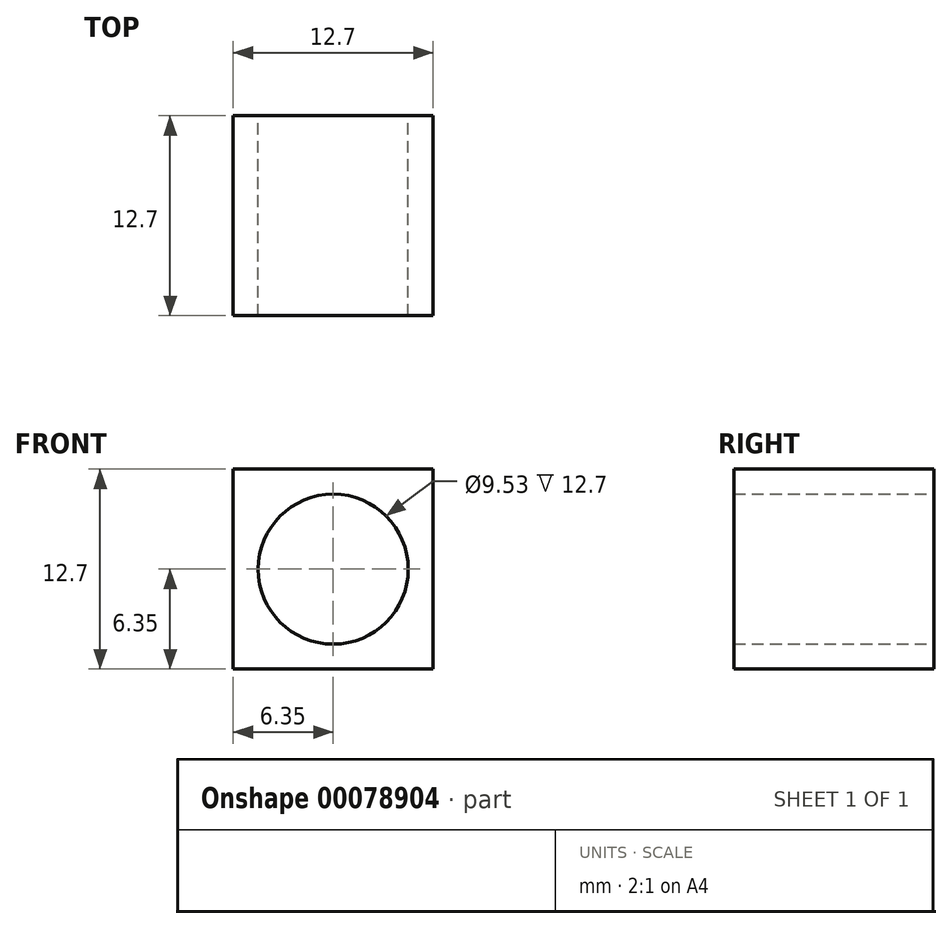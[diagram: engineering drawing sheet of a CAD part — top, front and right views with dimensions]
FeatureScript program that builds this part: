
annotation { "Feature Type Name" : "Feature", "Feature Type Description" : "" }
export const myFeature = defineFeature(function(context is Context, id is Id, definition is map)
    precondition{}
    {
        {
            var Q0;
            Q0=qCreatedBy(makeId("Front.planeOp"),FACE);
            var sketch = newSketch(context, id + "F0", { "sketchPlane" : qUnion([Q0])});
            skLineSegment(sketch, "E0.bottom", {"start": v(-6.35, 6.35) * mm, "end": v(6.35, 6.35) * mm});
            skLineSegment(sketch, "E0.top", {"start": v(-6.35, -6.35) * mm, "end": v(6.35, -6.35) * mm});
            skLineSegment(sketch, "E0.left", {"start": v(-6.35, 6.35) * mm, "end": v(-6.35, -6.35) * mm});
            skLineSegment(sketch, "E0.right", {"start": v(6.35, 6.35) * mm, "end": v(6.35, -6.35) * mm});
            skPoint(sketch, "E0.middle", {"position": v(0, 0) * mm});
            skCircle(sketch, "E1", {"center": v(0, 0) * mm, "radius": 4.76 * mm});
            skSolve(sketch);
        }
        {
            var Q0;
            Q0 = qSketchRegion(id + "F0", true);
            extrude(context, id + "F1", {"entities" : qUnion([Q0]), "depth" : 12.7 * mm});
        }
    });
